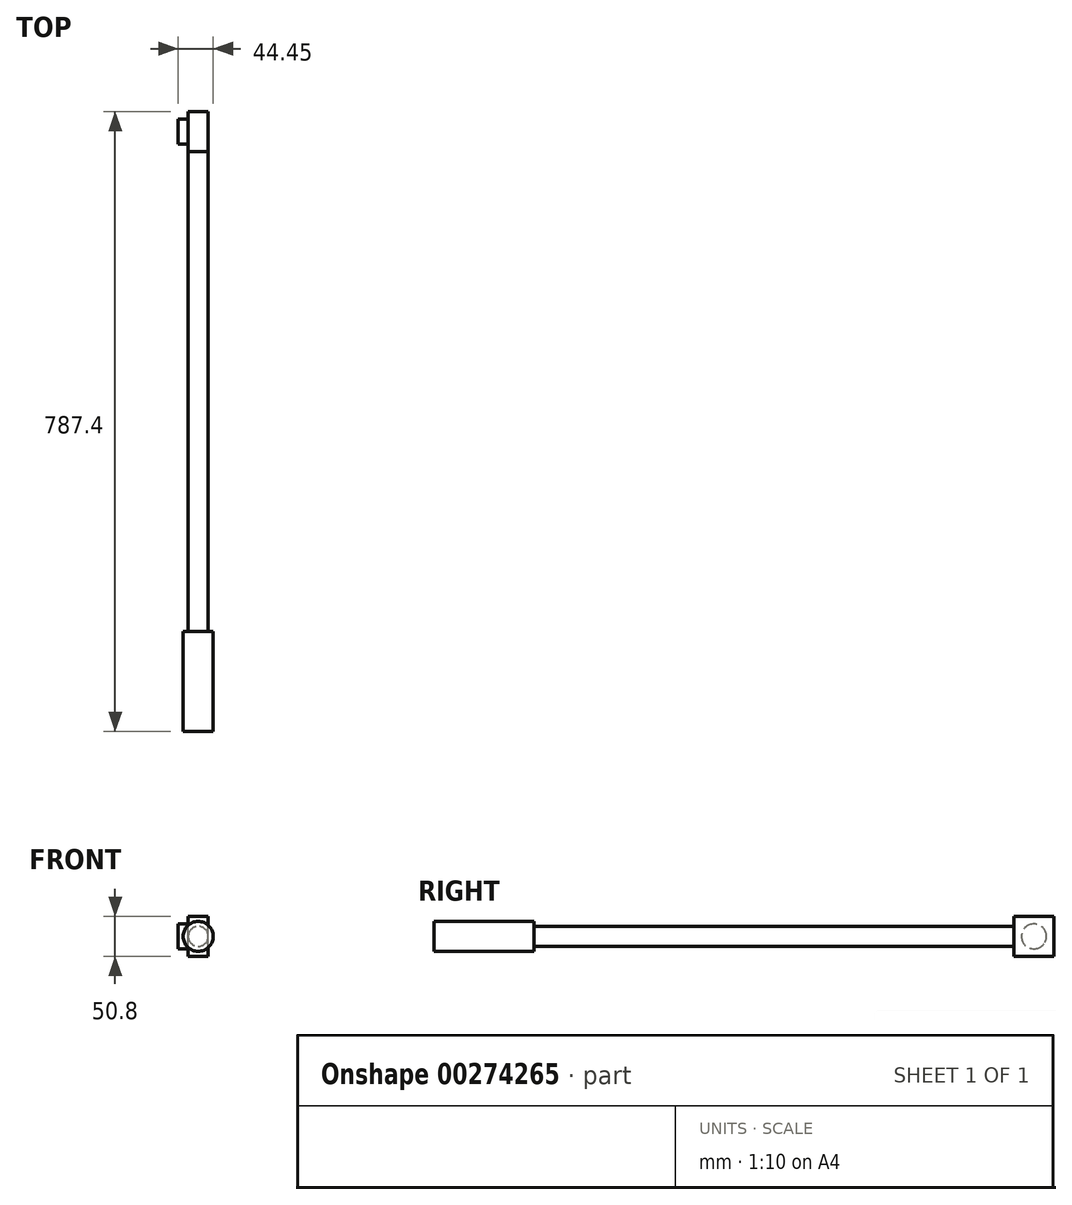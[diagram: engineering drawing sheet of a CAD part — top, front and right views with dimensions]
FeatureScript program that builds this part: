
annotation { "Feature Type Name" : "Feature", "Feature Type Description" : "" }
export const myFeature = defineFeature(function(context is Context, id is Id, definition is map)
    precondition{}
    {
        {
            var Q0;
            Q0=qCreatedBy(makeId("Front.planeOp"),FACE);
            var sketch = newSketch(context, id + "F0", { "sketchPlane" : qUnion([Q0])});
            skCircle(sketch, "E0", {"center": v(0, 0) * mm, "radius": 12.7 * mm});
            skSolve(sketch);
        }
        {
            var Q0;
            Q0=makeQuery(id+"F0.imprint","IMPRINT",FACE,{"disambiguationData":[TD([[makeQuery(id+"F0.imprint","IMPRINT",EDGE,{"derivedFrom":sQuery(id+"F0.wireOp",EDGE,"E0")}),1.0]])]});
            extrude(context, id + "F1", {"entities" : qUnion([Q0]), "depth" : 609.6 * mm});
        }
        {
            var Q0;
            Q0=makeQuery(id+"F1.opExtrude","CAP_FACE",FACE,{"disambiguationData":[OSD([sQuery(id+"F0.wireOp",EDGE,"E0")])],"isStart":false});
            var sketch = newSketch(context, id + "F2", { "sketchPlane" : qUnion([Q0])});
            skCircle(sketch, "E1", {"center": v(0, 0) * mm, "radius": 19.05 * mm});
            skSolve(sketch);
        }
        {
            var Q0;
            Q0=makeQuery(id+"F2.imprint","IMPRINT",FACE,{"disambiguationData":[TD([[makeQuery(id+"F2.imprint","IMPRINT",EDGE,{"derivedFrom":sQuery(id+"F2.wireOp",EDGE,"E1")}),1.0]])]});
            var Q1;
            Q1=makeQuery(id+"F2.imprint","IMPRINT",FACE,{"disambiguationData":[TD([[makeQuery(id+"F2.imprint","IMPRINT",EDGE,{"derivedFrom":makeQuery(id+"F1.opExtrude","CAP_EDGE",EDGE,{"disambiguationData":[OSD([sQuery(id+"F0.wireOp",EDGE,"E0")])],"isStart":false})}),1.0]])]});
            extrude(context, id + "F3", {"entities" : qUnion([Q0, Q1]), "operationType" : NewBodyOperationType.ADD, "depth" : 127 * mm});
        }
        {
            var Q0;
            Q0=qCreatedBy(makeId("Right.planeOp"),FACE);
            var sketch = newSketch(context, id + "F4", { "sketchPlane" : qUnion([Q0])});
            skLineSegment(sketch, "E2.bottom", {"start": v(0, -25.4) * mm, "end": v(50.8, -25.4) * mm});
            skLineSegment(sketch, "E2.top", {"start": v(0, 25.4) * mm, "end": v(50.8, 25.4) * mm});
            skLineSegment(sketch, "E2.left", {"start": v(0, -25.4) * mm, "end": v(0, 25.4) * mm});
            skLineSegment(sketch, "E2.right", {"start": v(50.8, -25.4) * mm, "end": v(50.8, 25.4) * mm});
            skSolve(sketch);
        }
        {
            var Q0;
            Q0=makeQuery(id+"F4.imprint","IMPRINT",FACE,{"disambiguationData":[TD([[makeQuery(id+"F4.imprint","IMPRINT",EDGE,{"derivedFrom":sQuery(id+"F4.wireOp",EDGE,"E2.bottom")}),1.0]])]});
            extrude(context, id + "F5", {"entities" : qUnion([Q0]), "operationType" : NewBodyOperationType.ADD, "endBound" : BoundingType.SYMMETRIC, "depth" : 25.4 * mm});
        }
        {
            var Q0;
            Q0=makeQuery(id+"F5.opExtrude","CAP_FACE",FACE,{"disambiguationData":[OSD([sQuery(id+"F4.wireOp",EDGE,"E2.bottom"),sQuery(id+"F4.wireOp",EDGE,"E2.top"),sQuery(id+"F4.wireOp",EDGE,"E2.left"),sQuery(id+"F4.wireOp",EDGE,"E2.right")])],"isStart":true});
            var sketch = newSketch(context, id + "F6", { "sketchPlane" : qUnion([Q0])});
            skCircle(sketch, "E3", {"center": v(-25.4, 0) * mm, "radius": 15.88 * mm});
            skSolve(sketch);
        }
        {
            var Q0;
            Q0=makeQuery(id+"F6.imprint","IMPRINT",FACE,{"disambiguationData":[TD([[makeQuery(id+"F6.imprint","IMPRINT",EDGE,{"derivedFrom":sQuery(id+"F6.wireOp",EDGE,"E3")}),1.0]])]});
            extrude(context, id + "F7", {"entities" : qUnion([Q0]), "operationType" : NewBodyOperationType.ADD, "depth" : 12.7 * mm});
        }
    });
